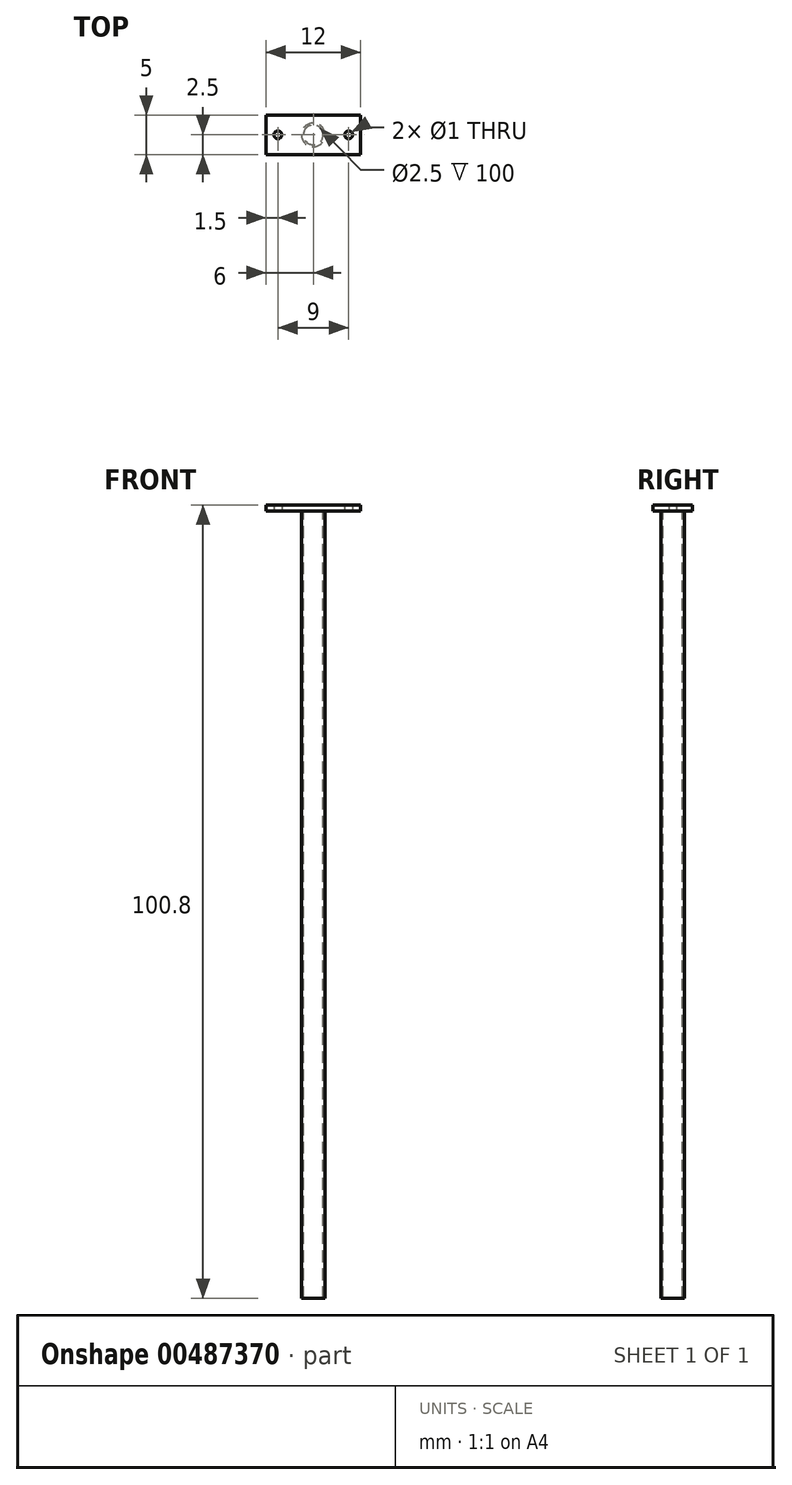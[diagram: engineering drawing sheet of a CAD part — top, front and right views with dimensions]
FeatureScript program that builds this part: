
annotation { "Feature Type Name" : "Feature", "Feature Type Description" : "" }
export const myFeature = defineFeature(function(context is Context, id is Id, definition is map)
    precondition{}
    {
        {
            var Q0;
            Q0=qCreatedBy(makeId("Top.planeOp"),FACE);
            var sketch = newSketch(context, id + "F0", { "sketchPlane" : qUnion([Q0])});
            skLineSegment(sketch, "E0.bottom", {"start": v(-6, 2.5) * mm, "end": v(6, 2.5) * mm});
            skLineSegment(sketch, "E0.top", {"start": v(-6, -2.5) * mm, "end": v(6, -2.5) * mm});
            skLineSegment(sketch, "E0.left", {"start": v(-6, 2.5) * mm, "end": v(-6, -2.5) * mm});
            skLineSegment(sketch, "E0.right", {"start": v(6, 2.5) * mm, "end": v(6, -2.5) * mm});
            skCircle(sketch, "E1", {"center": v(4.5, 0) * mm, "radius": 0.5 * mm});
            skCircle(sketch, "E2", {"center": v(-4.5, 0) * mm, "radius": 0.5 * mm});
            skSolve(sketch);
        }
        {
            var Q0;
            Q0 = qSketchRegion(id + "F0", true);
            extrude(context, id + "F1", {"entities" : qUnion([Q0]), "depth" : 0.8 * mm});
        }
        {
            var Q0;
            Q0=qCreatedBy(makeId("Top.planeOp"),FACE);
            var sketch = newSketch(context, id + "F2", { "sketchPlane" : qUnion([Q0])});
            skCircle(sketch, "E3", {"center": v(0, 0) * mm, "radius": 1.5 * mm});
            skCircle(sketch, "E4", {"center": v(0, 0) * mm, "radius": 1.25 * mm});
            skSolve(sketch);
        }
        {
            var Q0;
            Q0 = qSketchRegion(id + "F2", true);
            extrude(context, id + "F3", {"entities" : qUnion([Q0]), "operationType" : NewBodyOperationType.ADD, "oppositeDirection" : true, "depth" : 100 * mm});
        }
    });
